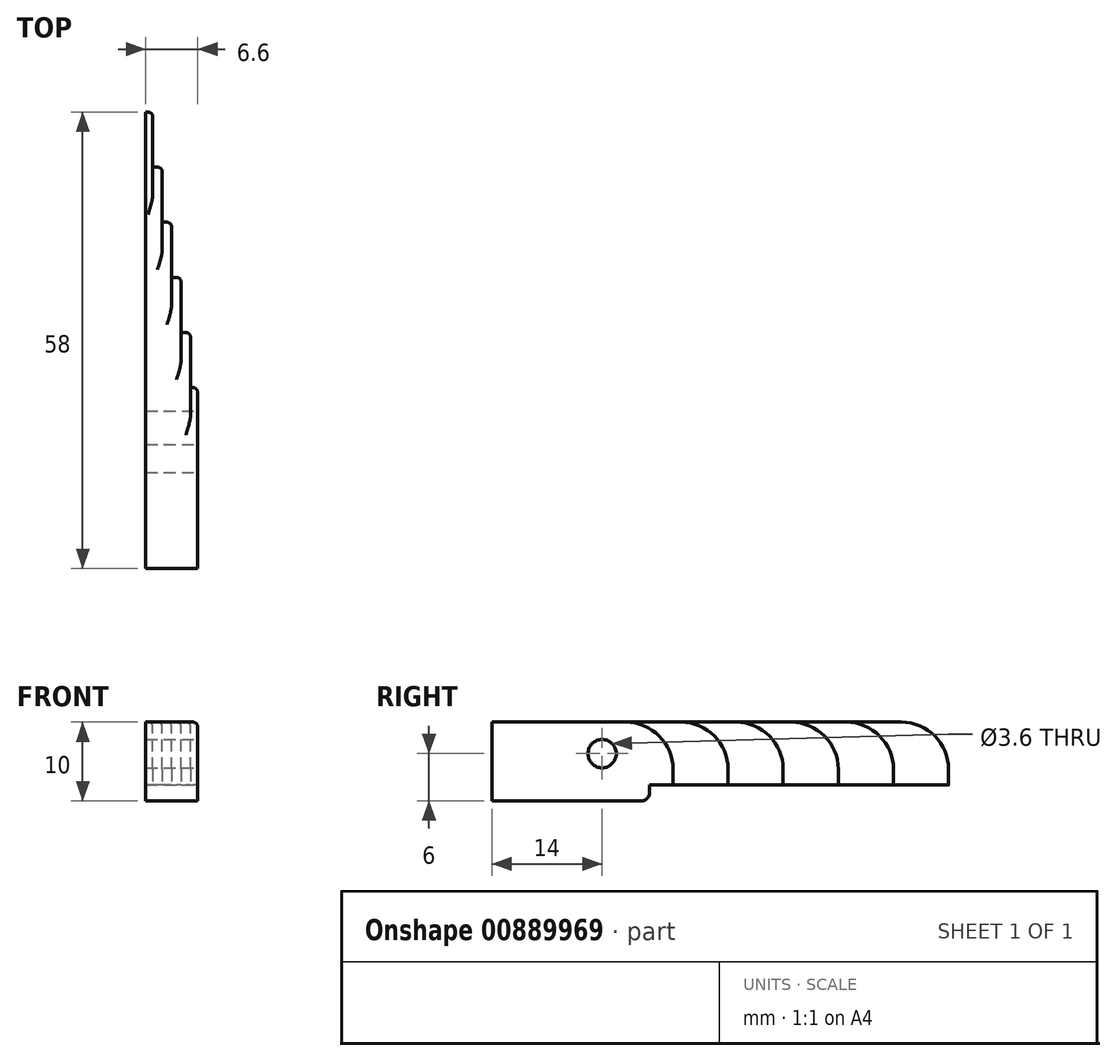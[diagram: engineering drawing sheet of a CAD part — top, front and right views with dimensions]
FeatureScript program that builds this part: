
annotation { "Feature Type Name" : "Feature", "Feature Type Description" : "" }
export const myFeature = defineFeature(function(context is Context, id is Id, definition is map)
    precondition{}
    {
        {
            var Q0;
            Q0=qCreatedBy(makeId("Top.planeOp"),FACE);
            var sketch = newSketch(context, id + "F0", { "sketchPlane" : qUnion([Q0])});
            skLineSegment(sketch, "E0.bottom", {"start": v(3.3, -29) * mm, "end": v(-3.3, -29) * mm});
            skLineSegment(sketch, "E0.top", {"start": v(-2.4, 29) * mm, "end": v(-3.3, 29) * mm});
            skLineSegment(sketch, "E0.left", {"start": v(3.3, -29) * mm, "end": v(3.3, -6) * mm});
            skLineSegment(sketch, "E0.right", {"start": v(-3.3, -29) * mm, "end": v(-3.3, 29) * mm});
            skPoint(sketch, "E0.middle", {"position": v(0, 0) * mm});
            skLineSegment(sketch, "E1.top", {"start": v(0, 15) * mm, "end": v(-1.2, 15) * mm});
            skLineSegment(sketch, "E1.right", {"start": v(-1.2, 22) * mm, "end": v(-1.2, 15) * mm});
            skLineSegment(sketch, "E2.top", {"start": v(-1.2, 22) * mm, "end": v(-2.4, 22) * mm});
            skLineSegment(sketch, "E2.right", {"start": v(-2.4, 29) * mm, "end": v(-2.4, 22) * mm});
            skLineSegment(sketch, "E3.top", {"start": v(0, 8) * mm, "end": v(1.2, 8) * mm});
            skLineSegment(sketch, "E3.left", {"start": v(0, 15) * mm, "end": v(0, 8) * mm});
            skLineSegment(sketch, "E4.top", {"start": v(1.2, 1) * mm, "end": v(2.4, 1) * mm});
            skLineSegment(sketch, "E4.left", {"start": v(1.2, 8) * mm, "end": v(1.2, 1) * mm});
            skLineSegment(sketch, "E5", {"start": v(2.4, 1) * mm, "end": v(2.4, -6) * mm});
            skLineSegment(sketch, "E6", {"start": v(2.4, -6) * mm, "end": v(3.3, -6) * mm});
            skPoint(sketch, "E7.orphan", {"position": v(3.3, 29) * mm});
            skPoint(sketch, "E8.orphan", {"position": v(0, 29) * mm});
            skLineSegment(sketch, "E9", {"start": v(-3.3, -29) * mm, "end": v(-3.3, -15) * mm});
            skLineSegment(sketch, "E10", {"start": v(-3.3, -15) * mm, "end": v(3.3, -15) * mm});
            skSolve(sketch);
        }
        {
            var Q0;
            Q0 = qSketchRegion(id + "F0", true);
            extrude(context, id + "F1", {"entities" : qUnion([Q0]), "depth" : 8 * mm, "offsetDistance" : 25 * mm});
        }
        {
            var Q0;
            {var subQ0=sQuery(id+"F0.wireOp",EDGE,"E0.bottom");Q0=makeQuery(id+"F0.imprint","IMPRINT",FACE,{"disambiguationData":[TD([[makeQuery(id+"F0.imprint","IMPRINT",EDGE,{"derivedFrom":subQ0}),-1.0]])]});}
            extrude(context, id + "F2", {"entities" : qUnion([Q0]), "operationType" : NewBodyOperationType.ADD, "oppositeDirection" : true, "depth" : 2 * mm, "offsetDistance" : 25 * mm});
        }
        {
            var Q0;
            {var subQ0=sQuery(id+"F0.wireOp",EDGE,"E0.left");Q0=makeQuery(id+"F2.boolean.opBoolean","MERGE",FACE,{"derivedFrom":[makeQuery(id+"F1.opExtrude","SWEPT_FACE",FACE,{"disambiguationData":[OSD([subQ0])]}),makeQuery(id+"F2.opExtrude","SWEPT_FACE",FACE,{"disambiguationData":[OSD([subQ0])]})]});}
            var sketch = newSketch(context, id + "F3", { "sketchPlane" : qUnion([Q0])});
            skCircle(sketch, "E11", {"center": v(-15, 4) * mm, "radius": 1.8 * mm});
            skSolve(sketch);
        }
        {
            var Q0;
            Q0=makeQuery(id+"F3.imprint","IMPRINT",FACE,{"disambiguationData":[TD([[makeQuery(id+"F3.imprint","IMPRINT",EDGE,{"derivedFrom":sQuery(id+"F3.wireOp",EDGE,"E11")}),1.0]])]});
            extrude(context, id + "F4", {"entities" : qUnion([Q0]), "operationType" : NewBodyOperationType.REMOVE, "oppositeDirection" : true, "depth" : 6.6 * mm, "offsetDistance" : 25 * mm});
        }
        {
            var Q0;
            Q0=makeQuery(id+"F1.opExtrude","CAP_EDGE",EDGE,{"disambiguationData":[OSD([sQuery(id+"F0.wireOp",EDGE,"E6")])],"isStart":false});
            var Q1;
            Q1=makeQuery(id+"F1.opExtrude","CAP_EDGE",EDGE,{"disambiguationData":[OSD([sQuery(id+"F0.wireOp",EDGE,"E4.top")])],"isStart":false});
            var Q2;
            Q2=makeQuery(id+"F1.opExtrude","CAP_EDGE",EDGE,{"disambiguationData":[OSD([sQuery(id+"F0.wireOp",EDGE,"E3.top")])],"isStart":false});
            var Q3;
            Q3=makeQuery(id+"F1.opExtrude","CAP_EDGE",EDGE,{"disambiguationData":[OSD([sQuery(id+"F0.wireOp",EDGE,"E1.top")])],"isStart":false});
            var Q4;
            Q4=makeQuery(id+"F1.opExtrude","CAP_EDGE",EDGE,{"disambiguationData":[OSD([sQuery(id+"F0.wireOp",EDGE,"E2.top")])],"isStart":false});
            var Q5;
            Q5=makeQuery(id+"F1.opExtrude","CAP_EDGE",EDGE,{"disambiguationData":[OSD([sQuery(id+"F0.wireOp",EDGE,"E0.top")])],"isStart":false});
            fillet(context, id + "F5", {"entities" : qUnion([Q0, Q1, Q2, Q3, Q4, Q5]), "radius" : 6 * mm, "tangentPropagation" : true, "allowEdgeOverflow" : false});
        }
        {
            var Q0;
            {var subQ0=sQuery(id+"F0.wireOp",EDGE,"E0.left");Q0=makeQuery(id+"F5.opFillet","BLEND_EDGE",EDGE,{"blendedFrom":[makeQuery(id+"F1.opExtrude","CAP_EDGE",EDGE,{"disambiguationData":[OSD([sQuery(id+"F0.wireOp",EDGE,"E6")])],"isStart":false}),makeQuery(id+"F2.boolean.opBoolean","MERGE",FACE,{"derivedFrom":[makeQuery(id+"F1.opExtrude","SWEPT_FACE",FACE,{"disambiguationData":[OSD([subQ0])]}),makeQuery(id+"F2.opExtrude","SWEPT_FACE",FACE,{"disambiguationData":[OSD([subQ0])]})]})],"blendedInto":[makeQuery(id+"F2.boolean.opBoolean","MERGE",FACE,{"derivedFrom":[makeQuery(id+"F1.opExtrude","SWEPT_FACE",FACE,{"disambiguationData":[OSD([subQ0])]}),makeQuery(id+"F2.opExtrude","SWEPT_FACE",FACE,{"disambiguationData":[OSD([subQ0])]})]})]});}
            var Q1;
            Q1=makeQuery(id+"F5.opFillet","BLEND_EDGE",EDGE,{"blendedFrom":[makeQuery(id+"F1.opExtrude","CAP_EDGE",EDGE,{"disambiguationData":[OSD([sQuery(id+"F0.wireOp",EDGE,"E4.top")])],"isStart":false}),makeQuery(id+"F1.opExtrude","SWEPT_FACE",FACE,{"disambiguationData":[OSD([sQuery(id+"F0.wireOp",EDGE,"E5")])]})],"blendedInto":[makeQuery(id+"F1.opExtrude","SWEPT_FACE",FACE,{"disambiguationData":[OSD([sQuery(id+"F0.wireOp",EDGE,"E5")])]})]});
            var Q2;
            Q2=makeQuery(id+"F5.opFillet","BLEND_EDGE",EDGE,{"blendedFrom":[makeQuery(id+"F1.opExtrude","CAP_EDGE",EDGE,{"disambiguationData":[OSD([sQuery(id+"F0.wireOp",EDGE,"E3.top")])],"isStart":false}),makeQuery(id+"F1.opExtrude","SWEPT_FACE",FACE,{"disambiguationData":[OSD([sQuery(id+"F0.wireOp",EDGE,"E4.left")])]})],"blendedInto":[makeQuery(id+"F1.opExtrude","SWEPT_FACE",FACE,{"disambiguationData":[OSD([sQuery(id+"F0.wireOp",EDGE,"E4.left")])]})]});
            var Q3;
            Q3=makeQuery(id+"F5.opFillet","BLEND_EDGE",EDGE,{"blendedFrom":[makeQuery(id+"F1.opExtrude","CAP_EDGE",EDGE,{"disambiguationData":[OSD([sQuery(id+"F0.wireOp",EDGE,"E1.top")])],"isStart":false}),makeQuery(id+"F1.opExtrude","SWEPT_FACE",FACE,{"disambiguationData":[OSD([sQuery(id+"F0.wireOp",EDGE,"E3.left")])]})],"blendedInto":[makeQuery(id+"F1.opExtrude","SWEPT_FACE",FACE,{"disambiguationData":[OSD([sQuery(id+"F0.wireOp",EDGE,"E3.left")])]})]});
            var Q4;
            Q4=makeQuery(id+"F5.opFillet","BLEND_EDGE",EDGE,{"blendedFrom":[makeQuery(id+"F1.opExtrude","CAP_EDGE",EDGE,{"disambiguationData":[OSD([sQuery(id+"F0.wireOp",EDGE,"E2.top")])],"isStart":false}),makeQuery(id+"F1.opExtrude","SWEPT_FACE",FACE,{"disambiguationData":[OSD([sQuery(id+"F0.wireOp",EDGE,"E1.right")])]})],"blendedInto":[makeQuery(id+"F1.opExtrude","SWEPT_FACE",FACE,{"disambiguationData":[OSD([sQuery(id+"F0.wireOp",EDGE,"E1.right")])]})]});
            var Q5;
            Q5=makeQuery(id+"F5.opFillet","BLEND_EDGE",EDGE,{"blendedFrom":[makeQuery(id+"F1.opExtrude","CAP_EDGE",EDGE,{"disambiguationData":[OSD([sQuery(id+"F0.wireOp",EDGE,"E0.top")])],"isStart":false}),makeQuery(id+"F1.opExtrude","SWEPT_FACE",FACE,{"disambiguationData":[OSD([sQuery(id+"F0.wireOp",EDGE,"E2.right")])]})],"blendedInto":[makeQuery(id+"F1.opExtrude","SWEPT_FACE",FACE,{"disambiguationData":[OSD([sQuery(id+"F0.wireOp",EDGE,"E2.right")])]})]});
            fillet(context, id + "F6", {"entities" : qUnion([Q0, Q1, Q2, Q3, Q4, Q5]), "radius" : .6 * mm, "tangentPropagation" : true, "allowEdgeOverflow" : false});
        }
        {
            var Q0;
            Q0=makeQuery(id+"F2.opExtrude","SWEPT_FACE",FACE,{"disambiguationData":[OSD([sQuery(id+"F0.wireOp",EDGE,"E10")])]});
            extrude(context, id + "F7", {"entities" : qUnion([Q0]), "operationType" : NewBodyOperationType.ADD, "depth" : 6 * mm, "offsetDistance" : 25 * mm});
        }
        {
            var Q0;
            {var subQ0=sQuery(id+"F0.wireOp",EDGE,"E10");Q0=makeQuery(id+"F7.opExtrude","CAP_EDGE",EDGE,{"disambiguationData":[OSD([subQ0]),TDD([makeQuery(id+"F2.opExtrude","CAP_EDGE",EDGE,{"disambiguationData":[OSD([subQ0])],"isStart":false})])],"isStart":false});}
            fillet(context, id + "F8", {"entities" : qUnion([Q0]), "radius" : 1 * mm, "tangentPropagation" : true, "allowEdgeOverflow" : false});
        }
    });
